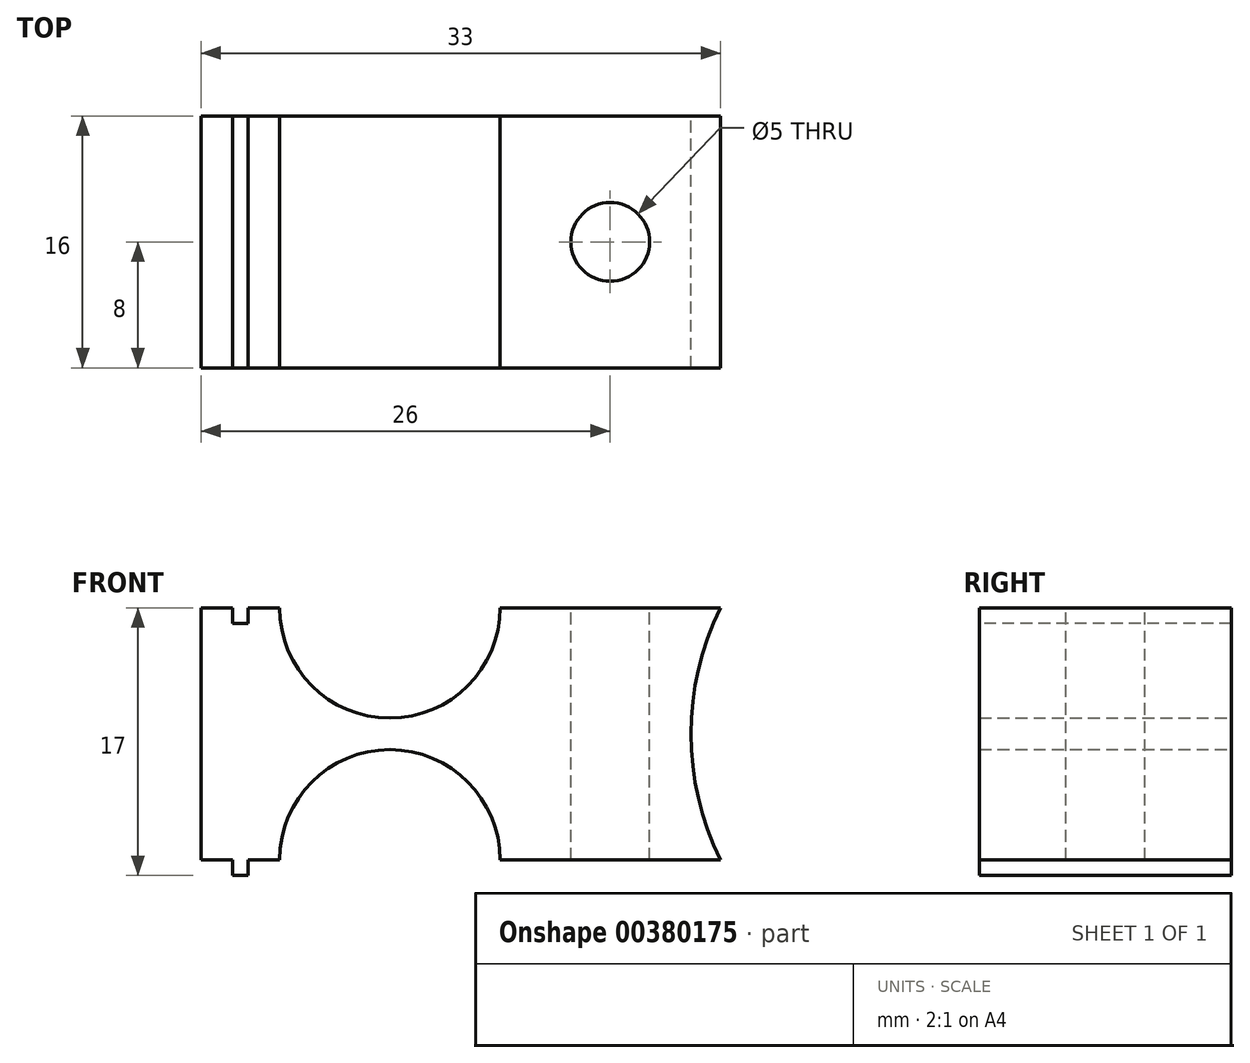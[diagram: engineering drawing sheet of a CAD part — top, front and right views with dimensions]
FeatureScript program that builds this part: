
annotation { "Feature Type Name" : "Feature", "Feature Type Description" : "" }
export const myFeature = defineFeature(function(context is Context, id is Id, definition is map)
    precondition{}
    {
        {
            var Q0;
            Q0=qCreatedBy(makeId("Front.planeOp"),FACE);
            var sketch = newSketch(context, id + "F0", { "sketchPlane" : qUnion([Q0])});
            skLineSegment(sketch, "E0", {"start": v(-21, -8) * mm, "end": v(-21, 8) * mm});
            skLineSegment(sketch, "E1", {"start": v(-21, 8) * mm, "end": v(-16, 8) * mm});
            skArc(sketch, "E2", {"start": v(-16, 8) * mm, "mid": v(-9, 1) * mm, "end": v(-2, 8) * mm});
            skLineSegment(sketch, "E3", {"start": v(-2, 8) * mm, "end": v(12, 8) * mm});
            skLineSegment(sketch, "E4", {"start": v(12, -8) * mm, "end": v(-2, -8) * mm});
            skArc(sketch, "E5", {"start": v(-2, -8) * mm, "mid": v(-9, -1) * mm, "end": v(-16, -8) * mm});
            skLineSegment(sketch, "E6", {"start": v(-21, -8) * mm, "end": v(-16, -8) * mm});
            skArc(sketch, "E7", {"start": v(12, 8) * mm, "mid": v(10.12, 0) * mm, "end": v(12, -8) * mm});
            skSolve(sketch);
        }
        {
            var Q0;
            Q0=makeQuery(id+"F0.imprint","IMPRINT",FACE,{"disambiguationData":[TD([[makeQuery(id+"F0.imprint","IMPRINT",EDGE,{"derivedFrom":sQuery(id+"F0.wireOp",EDGE,"E0")}),-1.0]])]});
            extrude(context, id + "F1", {"entities" : qUnion([Q0]), "depth" : 16 * mm});
        }
        {
            var Q0;
            Q0=makeQuery(id+"F1.opExtrude","SWEPT_FACE",FACE,{"disambiguationData":[OSD([sQuery(id+"F0.wireOp",EDGE,"E3")])]});
            var sketch = newSketch(context, id + "F2", { "sketchPlane" : qUnion([Q0])});
            skPoint(sketch, "E8", {"position": v(5, -8) * mm});
            skSolve(sketch);
        }
        {
            var Q0;
            Q0=sQuery(id+"F2.wireOp",VERTEX,"79e075bb-6bfb-49c5-8b4c-a002d3132a17");
            var Q1;
            Q1=sQuery(id+"F2.wireOp",VERTEX,"E8");
            var Q2;
            Q2=makeQuery(id+"F1.opExtrude","SWEPT_BODY",BODY,{"disambiguationData":[OSD([sQuery(id+"F0.wireOp",EDGE,"E0"),sQuery(id+"F0.wireOp",EDGE,"E1"),sQuery(id+"F0.wireOp",EDGE,"E2"),sQuery(id+"F0.wireOp",EDGE,"E3"),sQuery(id+"F0.wireOp",EDGE,"WODfPS9L-Gdiw-NReB-O732-VzQiCiSEnpou"),sQuery(id+"F0.wireOp",EDGE,"E4"),sQuery(id+"F0.wireOp",EDGE,"E5"),sQuery(id+"F0.wireOp",EDGE,"E6")])]});
            hole(context, id + "F3", {"style" : HoleStyle.SIMPLE, "endStyle" : HoleEndStyle.THROUGH, "holeDiameter" : 5 * mm, "isTappedThrough" : true, "tappedDepth" : 12.7 * mm, "tapClearance" : 3, "locations" : qUnion([Q0, Q1]), "scope" : qUnion([Q2])});
        }
        {
            var Q0;
            Q0=makeQuery(id+"F1.opExtrude","SWEPT_FACE",FACE,{"disambiguationData":[OSD([sQuery(id+"F0.wireOp",EDGE,"E1")])]});
            var sketch = newSketch(context, id + "F4", { "sketchPlane" : qUnion([Q0])});
            skLineSegment(sketch, "E9.bottom", {"start": v(-19, 0) * mm, "end": v(-18, 0) * mm});
            skLineSegment(sketch, "E9.top", {"start": v(-19, -16) * mm, "end": v(-18, -16) * mm});
            skLineSegment(sketch, "E9.left", {"start": v(-19, 0) * mm, "end": v(-19, -16) * mm});
            skLineSegment(sketch, "E9.right", {"start": v(-18, 0) * mm, "end": v(-18, -16) * mm});
            skSolve(sketch);
        }
        {
            var Q0;
            Q0=makeQuery(id+"F4.imprint","IMPRINT",FACE,{"disambiguationData":[TD([[makeQuery(id+"F4.imprint","IMPRINT",EDGE,{"derivedFrom":sQuery(id+"F4.wireOp",EDGE,"E9.bottom")}),-1.0]])]});
            extrude(context, id + "F5", {"entities" : qUnion([Q0]), "operationType" : NewBodyOperationType.REMOVE, "oppositeDirection" : true, "depth" : 1 * mm, "offsetDistance" : 25 * mm});
        }
        {
            var Q0;
            Q0=makeQuery(id+"F1.opExtrude","SWEPT_FACE",FACE,{"disambiguationData":[OSD([sQuery(id+"F0.wireOp",EDGE,"E6")])]});
            var sketch = newSketch(context, id + "F6", { "sketchPlane" : qUnion([Q0])});
            skLineSegment(sketch, "E10.bottom", {"start": v(-19, 16) * mm, "end": v(-18, 16) * mm});
            skLineSegment(sketch, "E10.top", {"start": v(-19, 0) * mm, "end": v(-18, 0) * mm});
            skLineSegment(sketch, "E10.left", {"start": v(-19, 16) * mm, "end": v(-19, 0) * mm});
            skLineSegment(sketch, "E10.right", {"start": v(-18, 16) * mm, "end": v(-18, 0) * mm});
            skSolve(sketch);
        }
        {
            var Q0;
            Q0=makeQuery(id+"F6.imprint","IMPRINT",FACE,{"disambiguationData":[TD([[makeQuery(id+"F6.imprint","IMPRINT",EDGE,{"derivedFrom":sQuery(id+"F6.wireOp",EDGE,"E10.bottom")}),-1.0]])]});
            extrude(context, id + "F7", {"entities" : qUnion([Q0]), "operationType" : NewBodyOperationType.ADD, "depth" : 1 * mm, "offsetDistance" : 25 * mm});
        }
    });
